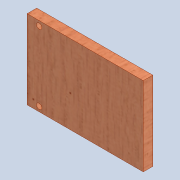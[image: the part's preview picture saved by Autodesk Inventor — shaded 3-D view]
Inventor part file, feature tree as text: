
AUTODESK INVENTOR PART (.ipt)
format: ipt  version: 2020 (Build 240168000, 168)  size: 117,248 bytes
history: native  units: mm
features: sketch x2, extrude x1, hole x1
ambient origin geometry x8: Origin, YZ Plane, XZ Plane, XY Plane, X Axis, Y Axis, Z Axis, Center Point
bodies: Solid1 (feature_tree)
feature tree (4):
  extrude  "Extrusion1"  Depth=66.0mm
  hole  "Hole1"  [1 undecoded]
  sketch  "Sketch1"  dims[d0=97.0mm d1=66.0mm]
  sketch  "Sketch4"  dims[d2=8.0mm d3=0.0mm d19=10.0mm d20=4.0mm d21=4.0mm d22=4.5mm d23=6.0mm d24=4.0mm d25=2.0mm d26=90.0deg d27=8.0mm d28=20.594885mm]
note: 1 required parameter value undecoded (feature->parameter linkage not recoverable at this tier; creation-order binding heuristic only, values carry confidence <= 0.55)
